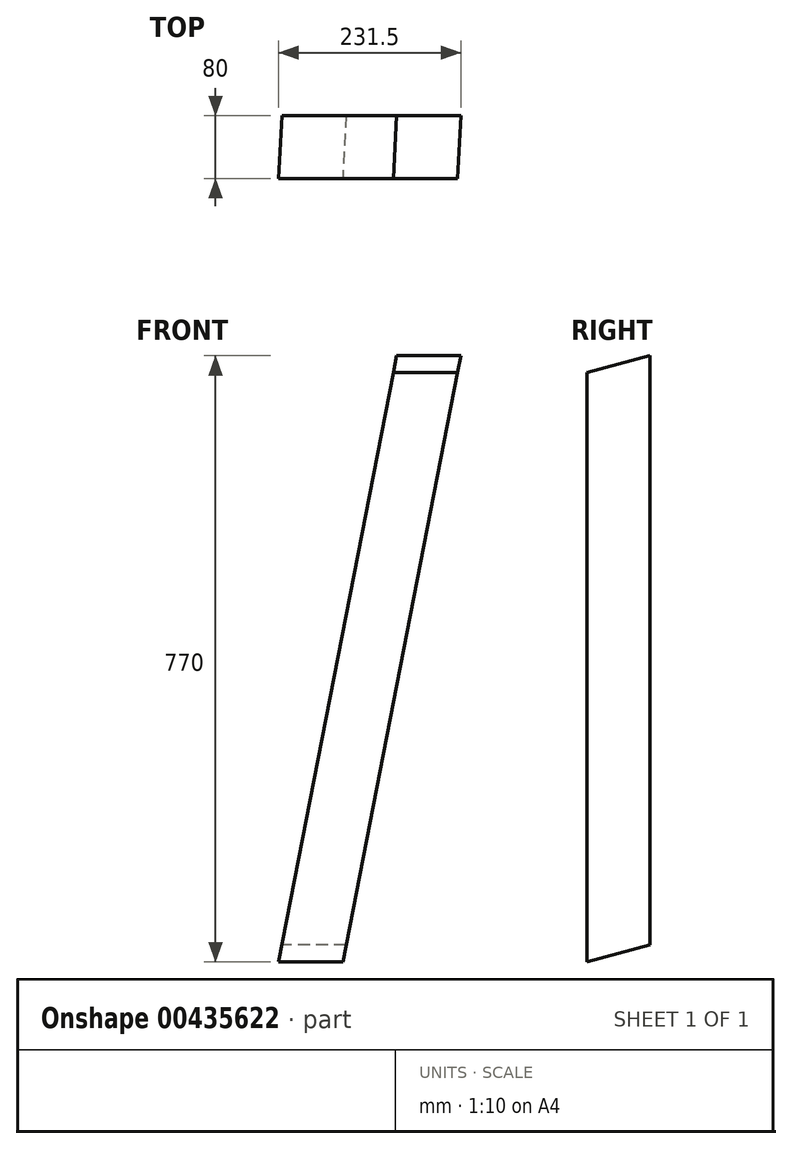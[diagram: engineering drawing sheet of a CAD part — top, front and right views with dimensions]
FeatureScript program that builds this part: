
annotation { "Feature Type Name" : "Feature", "Feature Type Description" : "" }
export const myFeature = defineFeature(function(context is Context, id is Id, definition is map)
    precondition{}
    {
        {
            var Q0;
            Q0=qCreatedBy(makeId("Front.planeOp"),FACE);
            var sketch = newSketch(context, id + "F0", { "sketchPlane" : qUnion([Q0])});
            skLineSegment(sketch, "E0", {"start": v(0, 1049.16) * mm, "end": v(0, -1171.87) * mm, "construction": true});
            skLineSegment(sketch, "E1", {"start": v(-1079.84, 0) * mm, "end": v(1092.11, 0) * mm, "construction": true});
            skLineSegment(sketch, "E2", {"start": v(-582.87, 770) * mm, "end": v(1224.02, 770) * mm, "construction": true});
            skLineSegment(sketch, "E3", {"start": v(150, 962.7) * mm, "end": v(150, 418.92) * mm, "construction": true});
            skLineSegment(sketch, "E4", {"start": v(0, 0) * mm, "end": v(150, 770) * mm});
            skLineSegment(sketch, "E5", {"start": v(2.98, 15.3) * mm, "end": v(81.5, 0) * mm, "construction": true});
            skLineSegment(sketch, "E6", {"start": v(81.5, 0) * mm, "end": v(186.6, 539.51) * mm, "construction": true});
            skLineSegment(sketch, "E7", {"start": v(81.5, 0) * mm, "end": v(231.5, 770) * mm});
            skLineSegment(sketch, "E8", {"start": v(81.5, 0) * mm, "end": v(0, 0) * mm});
            skLineSegment(sketch, "E9", {"start": v(231.5, 770) * mm, "end": v(150, 770) * mm});
            skSolve(sketch);
        }
        {
            var Q0;
            Q0 = qSketchRegion(id + "F0", true);
            extrude(context, id + "F1", {"entities" : qUnion([Q0]), "oppositeDirection" : true, "depth" : 80 * mm});
        }
        {
            var Q0;
            Q0=qCreatedBy(makeId("Right.planeOp"),FACE);
            var sketch = newSketch(context, id + "F2", { "sketchPlane" : qUnion([Q0])});
            skLineSegment(sketch, "E10", {"start": v(0, 0) * mm, "end": v(192.56, 0) * mm, "construction": true});
            skLineSegment(sketch, "E11", {"start": v(0, 0) * mm, "end": v(170.24, 45.61) * mm});
            skLineSegment(sketch, "E12", {"start": v(170.24, 45.61) * mm, "end": v(170.24, 0) * mm});
            skLineSegment(sketch, "E13", {"start": v(170.24, 0) * mm, "end": v(0, 0) * mm});
            skLineSegment(sketch, "E14", {"start": v(0, 0) * mm, "end": v(0, 934.22) * mm, "construction": true});
            skLineSegment(sketch, "E15", {"start": v(359.61, 770) * mm, "end": v(-462, 770) * mm, "construction": true});
            skLineSegment(sketch, "E16", {"start": v(80, 779.53) * mm, "end": v(80, 742.5) * mm, "construction": true});
            skLineSegment(sketch, "E17", {"start": v(80, 770) * mm, "end": v(-16.42, 744.16) * mm});
            skLineSegment(sketch, "E18", {"start": v(-16.42, 744.16) * mm, "end": v(-16.42, 770) * mm});
            skLineSegment(sketch, "E19", {"start": v(-16.42, 770) * mm, "end": v(80, 770) * mm});
            skSolve(sketch);
        }
        {
            var Q0;
            Q0 = qSketchRegion(id + "F2", true);
            extrude(context, id + "F3", {"entities" : qUnion([Q0]), "operationType" : NewBodyOperationType.REMOVE, "depth" : 300 * mm});
        }
    });
